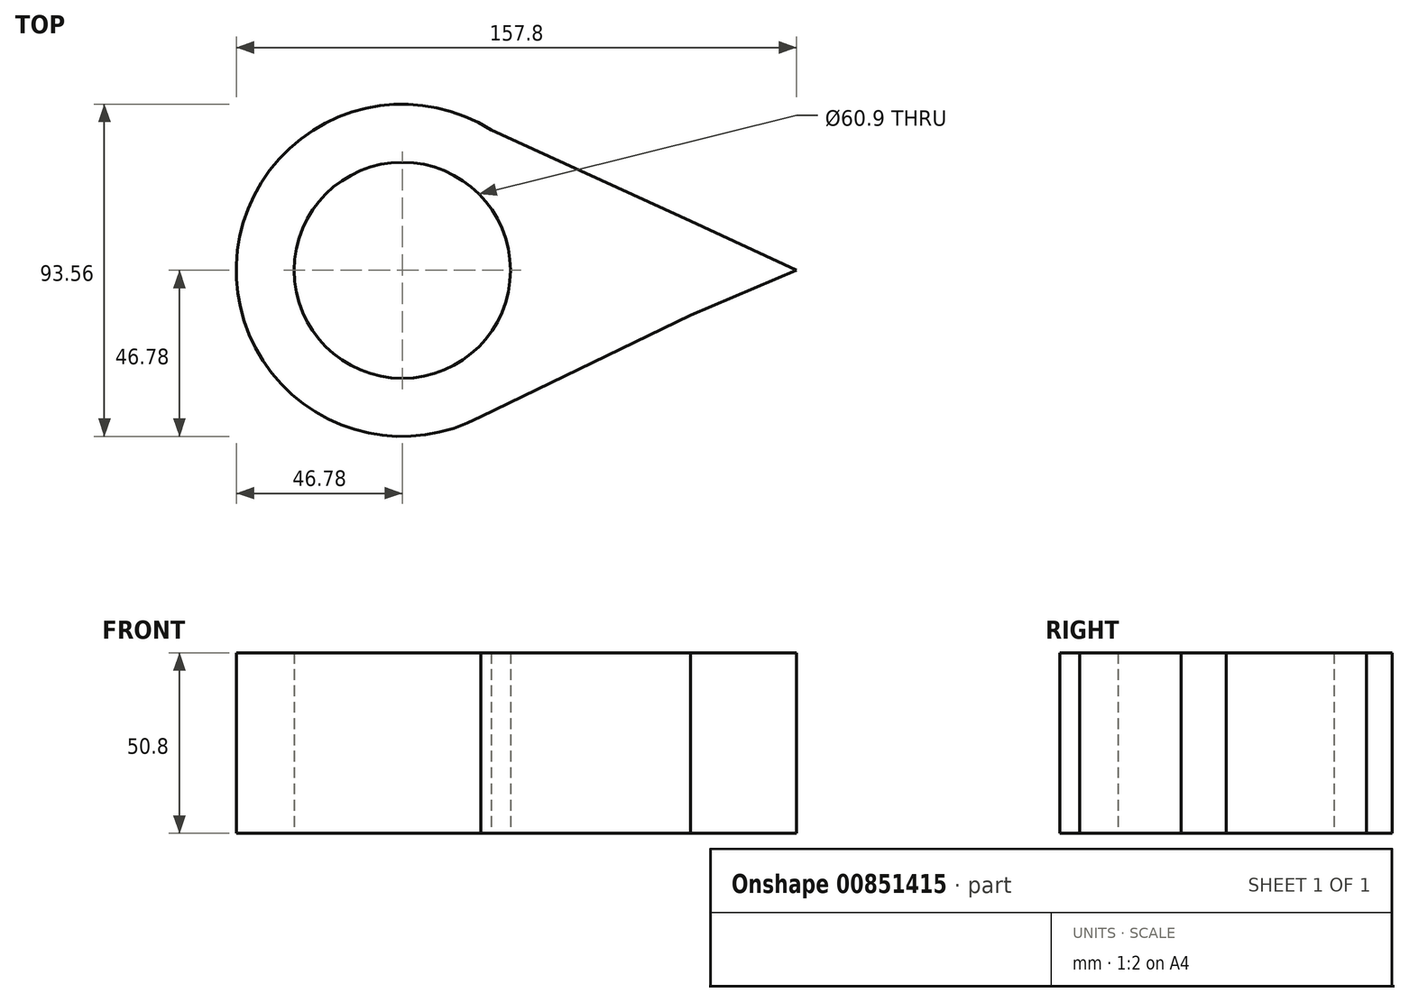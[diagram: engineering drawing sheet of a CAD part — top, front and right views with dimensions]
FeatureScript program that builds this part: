
annotation { "Feature Type Name" : "Feature", "Feature Type Description" : "" }
export const myFeature = defineFeature(function(context is Context, id is Id, definition is map)
    precondition{}
    {
        {
            var Q0;
            Q0=qCreatedBy(makeId("Top.planeOp"),FACE);
            var sketch = newSketch(context, id + "F0", { "sketchPlane" : qUnion([Q0])});
            skCircle(sketch, "E0", {"center": v(0, 0) * mm, "radius": 30.45 * mm});
            skCircle(sketch, "E1", {"center": v(0, 0) * mm, "radius": 46.78 * mm});
            skLineSegment(sketch, "E2", {"start": v(0, 0) * mm, "end": v(111.02, 0) * mm});
            skLineSegment(sketch, "E3", {"start": v(111.02, 0) * mm, "end": v(81.18, 13.87) * mm});
            skLineSegment(sketch, "E4", {"start": v(81.18, 13.87) * mm, "end": v(81.18, -12.62) * mm});
            skLineSegment(sketch, "E5", {"start": v(81.18, -12.62) * mm, "end": v(111.02, 0) * mm});
            skLineSegment(sketch, "E6", {"start": v(13.58, 44.77) * mm, "end": v(81.18, 13.87) * mm});
            skLineSegment(sketch, "E7", {"start": v(18.59, -42.93) * mm, "end": v(81.18, -12.62) * mm});
            skSolve(sketch);
        }
        {
            var Q0;
            Q0 = qSketchRegion(id + "F0", true);
            extrude(context, id + "F1", {"entities" : qUnion([Q0]), "depth" : 50.8 * mm, "offsetDistance" : 25.4 * mm});
        }
    });
